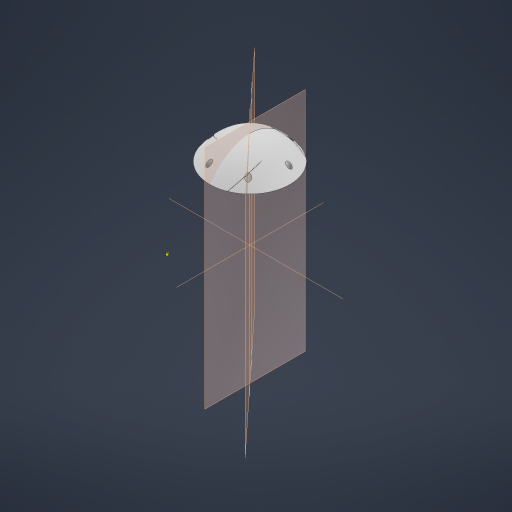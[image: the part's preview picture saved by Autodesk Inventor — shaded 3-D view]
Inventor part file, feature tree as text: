
AUTODESK INVENTOR PART (.ipt)
format: ipt  version: 2023 (Build 270158000, 158)  size: 1,769,984 bytes
history: native  units: mm
features: sketch x23, extrude x14, projected_geometry x11, reference x9, other x7, plane x6, pattern_circular x6, revolve x5, pattern_linear x2, sweep x1, chamfer x1, shell x1
ambient origin geometry x8: Origin, YZ Plane, XZ Plane, XY Plane, X Axis, Y Axis, Z Axis, Center Point
bodies: Solid1 (feature_tree)
feature tree (86):
  revolve  "Revolution1"  [1 undecoded]
  sketch  "3D Sketch1"
  plane  "Work Plane1"
  sweep  "Sweep1"
  pattern_circular  "Circular Pattern1"  Count=3 Angle=360.0deg
  extrude  "Extrusion1"  TaperAngle=0.0deg  [1 undecoded]
  revolve  "Revolution4"  [1 undecoded]
  extrude  "Extrusion9"  Depth=10.0mm
  plane  "Work Plane7"
  revolve  "Revolution5"  [1 undecoded]
  pattern_circular  "Circular Pattern6"  Count=3 Angle=360.0deg
  extrude  "Extrusion10"  Depth=6.0mm
  revolve  "Revolution6"  Angle=45.0deg
  pattern_circular  "Circular Pattern8"  Count=3 Angle=360.0deg
  extrude  "Extrusion12"  Depth=6.0mm
  extrude  "Extrusion13"  Depth=60.0mm TaperAngle=360.0deg
  extrude  "Extrusion14"  Depth=130.0mm
  extrude  "Extrusion15"  TaperAngle=90.0deg  [1 undecoded]
  extrude  "Extrusion16"  Depth=10.0mm
  pattern_linear  "Rectangular Pattern1"  Spacing1=4.0mm  [1 undecoded]
  pattern_linear  "Rectangular Pattern2"  Spacing1=5.0mm  [1 undecoded]
  plane  "Work Plane3"
  sketch  "Sketch12"  dims[d16=0.2mm]
  plane  "Work Plane6"
  extrude  "Extrusion6"  TaperAngle=90.0deg  [1 undecoded]
  chamfer  "Chamfer2"  Distance=60.0mm Angle=360.0deg
  pattern_circular  "Circular Pattern4"  [2 undecoded]
  shell  "Shell2"  Thickness=3.3mm
  extrude  "Extrusion8"  Depth=10.0mm TaperAngle=0.0deg
  extrude  "Extrusion2"  Depth=10.0mm
  sketch  "Sketch7"  dims[d13=1.6mm]
  plane  "Work Plane4"
  extrude  "Extrusion3"  Depth=10.0mm TaperAngle=0.0deg
  extrude  "Extrusion4"  Depth=10.0mm
  pattern_circular  "Circular Pattern2"  [2 undecoded]
  extrude  "Extrusion7"  Depth=10.0mm
  pattern_circular  "Circular Pattern5"  [2 undecoded]
  revolve  "Revolution2"  [1 undecoded]
  sketch  "Sketch1"  dims[d0=160.0mm d1=100.0mm]
  other  "Helical Curve2"
  other  "Project to Surface1"
  sketch  "Sketch2"  dims[d2=90.0deg d7=1200.0mm d8=637.649mm d9=252.623mm d10=0.0mm]
  sketch  "Sketch3"  dims[d11=15.0mm]
  plane  "Work Plane2"
  sketch  "Sketch6"  dims[d12=3.0mm]
  sketch  "Sketch8"  dims[d14=1.478932mm]
  sketch  "Sketch9"  dims[d15=0.2mm]
  sketch  "Sketch13"  dims[d17=0.2mm]
  sketch  "Sketch14"  dims[d18=0.0mm d19=0.0mm d20=30.0mm d21=360.0deg]
  reference  "Reference1"
  sketch  "Sketch15"  dims[d23=120.0mm d24=0.0mm d25=0.0mm]
  sketch  "Sketch16"  dims[d26=-130.0mm d27=-10.0mm d29=1.0mm]
  sketch  "Sketch18"  dims[d30=10.0mm d31=0.0mm d32=6.0mm]
  sketch  "Sketch19"  dims[d33=4.0mm d34=0.0mm d35=4.0mm]
  reference  "Reference3"
  reference  "Reference4"
  reference  "Reference5"
  reference  "Reference6"
  reference  "Reference7"
  reference  "Reference8"
  other  "Work Axis1"
  sketch  "Sketch20"  dims[d36=4.0mm d37=0.0mm d38=30.0mm d39=360.0deg]
  reference  "Reference9"
  sketch  "Sketch21"  dims[d51=100.0mm d52=6.0mm]
  reference  "Reference10"
  sketch  "Sketch24"  dims[d53=4.0mm d54=0.0mm d55=3.5mm d56=1.0mm d57=45.0deg d58=30.0mm d59=360.0deg]
  projected_geometry  "Projected Loop3"
  sketch  "Sketch25"  dims[d61=30.0deg d62=6.0mm]
  projected_geometry  "Projected Loop4"
  sketch  "Sketch26"  dims[d63=4.0mm d64=0.0mm d65=60.0mm d66=360.0deg]
  projected_geometry  "Projected Loop5"
  sketch  "Sketch27"  dims[d68=360.0deg d69=130.0mm]
  sketch  "Sketch28"  dims[d70=0.0mm d71=0.0mm d73=90.0deg]
  sketch  "Sketch31"  dims[d74=0.0mm d75=0.0mm d76=8.0mm d77=4.0mm d78=5.0mm d79=90.0deg d80=60.0mm d81=360.0deg d83=5.0mm d84=3.3mm d85=26.0mm d86=0.0mm d89=66.5mm d90=150.0mm d91=0.0mm d92=25.9mm d93=1.6mm d94=0.0mm d95=1.6mm d96=1.6mm d97=1.6mm d98=30.0mm d99=0.0mm d100=30.0mm d101=0.0mm d102=4.0mm d103=10.0mm d104=0.0mm d105=60.0mm d107=10.0mm d108=70.0mm d110=10.0mm d111=100.0mm d113=10.0mm d114=60.0mm d116=10.0mm d117=1.3mm d118=1.3mm d124=1.2mm d125=6.457718mm d126=30.0mm d127=360.0deg]
  projected_geometry  "Project Cut Edges1"
  projected_geometry  "Project Cut Edges2"
  projected_geometry  "Project Cut Edges3"
  projected_geometry  "Project Cut Edges5"
  projected_geometry  "Project Cut Edges6"
  parser-record x1  (decoder bookkeeping rows leaked as tree rows — omitted from the tree; the rows remain in map.json)
  other  "Assembly1.iam"
  other  "lower_centering_ring:1"
  projected_geometry  "Project Cut Edges7"
  projected_geometry  "Project Cut Edges9"
  other  "top_centering_ring:1"
  projected_geometry  "Project Cut Edges10"
note: 15 required parameter values undecoded (feature->parameter linkage not recoverable at this tier; creation-order binding heuristic only, values carry confidence <= 0.55)
note: 1 file-system path scrubbed to <path> (originals preserved in map.json)